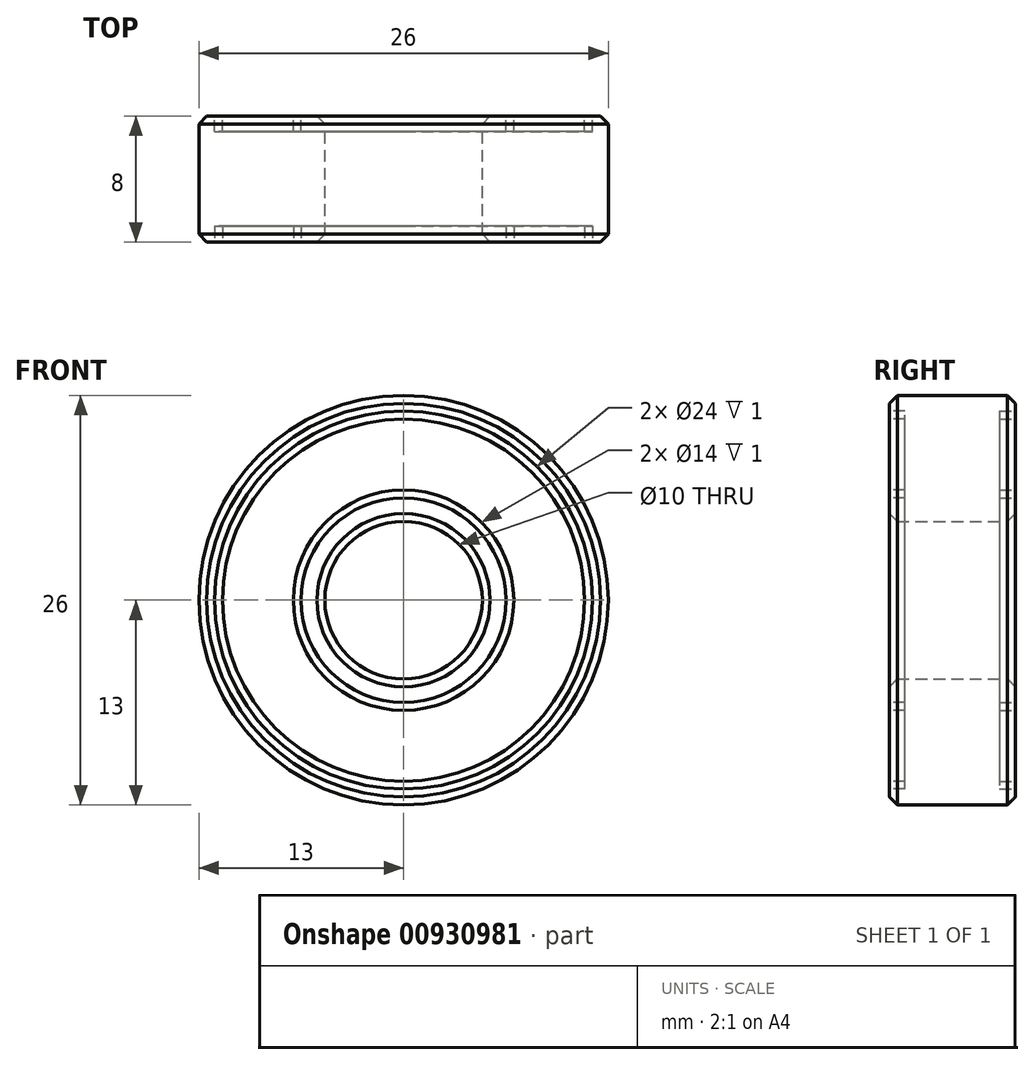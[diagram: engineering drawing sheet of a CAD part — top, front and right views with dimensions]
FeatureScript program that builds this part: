
annotation { "Feature Type Name" : "Feature", "Feature Type Description" : "" }
export const myFeature = defineFeature(function(context is Context, id is Id, definition is map)
    precondition{}
    {
        {
            var Q0;
            Q0=qCreatedBy(makeId("Front.planeOp"),FACE);
            var sketch = newSketch(context, id + "F0", { "sketchPlane" : qUnion([Q0])});
            skCircle(sketch, "E0", {"center": v(0, 0) * mm, "radius": 13 * mm});
            skCircle(sketch, "E1", {"center": v(0, 0) * mm, "radius": 5 * mm});
            skSolve(sketch);
        }
        {
            var Q0;
            Q0 = qSketchRegion(id + "F0", true);
            extrude(context, id + "F1", {"entities" : qUnion([Q0]), "depth" : 8 * mm, "offsetDistance" : 25 * mm});
        }
        {
            var Q0;
            Q0=makeQuery(id+"F1.opExtrude","CAP_FACE",FACE,{"disambiguationData":[OSD([sQuery(id+"F0.wireOp",EDGE,"E0"),sQuery(id+"F0.wireOp",EDGE,"E1")])],"isStart":false});
            var sketch = newSketch(context, id + "F2", { "sketchPlane" : qUnion([Q0])});
            skCircle(sketch, "E2", {"center": v(0, 0) * mm, "radius": 6.5 * mm});
            skCircle(sketch, "E3", {"center": v(0, 0) * mm, "radius": 7 * mm});
            skCircle(sketch, "E4", {"center": v(0, 0) * mm, "radius": 12 * mm});
            skCircle(sketch, "E5", {"center": v(0, 0) * mm, "radius": 11.5 * mm});
            skSolve(sketch);
        }
        {
            var Q0;
            Q0 = qSketchRegion(id + "F2", true);
            var Q1;
            Q1=makeQuery(id+"F2.imprint","IMPRINT",FACE,{"disambiguationData":[TD([[makeQuery(id+"F2.imprint","IMPRINT",EDGE,{"derivedFrom":sQuery(id+"F2.wireOp",EDGE,"E2")}),-1.0]])]});
            extrude(context, id + "F3", {"entities" : qUnion([Q0, Q1]), "operationType" : NewBodyOperationType.REMOVE, "oppositeDirection" : true, "depth" : 1 * mm, "offsetDistance" : 25 * mm});
        }
        {
            var Q0;
            Q0=makeQuery(id+"F1.opExtrude","CAP_FACE",FACE,{"disambiguationData":[OSD([sQuery(id+"F0.wireOp",EDGE,"E0"),sQuery(id+"F0.wireOp",EDGE,"E1")])],"isStart":true});
            var sketch = newSketch(context, id + "F4", { "sketchPlane" : qUnion([Q0])});
            skCircle(sketch, "E6", {"center": v(0, 0) * mm, "radius": 7 * mm});
            skCircle(sketch, "E7", {"center": v(0, 0) * mm, "radius": 6.5 * mm});
            skCircle(sketch, "E8", {"center": v(0, 0) * mm, "radius": 12 * mm});
            skCircle(sketch, "E9", {"center": v(0, 0) * mm, "radius": 11.5 * mm});
            skSolve(sketch);
        }
        {
            var Q0;
            Q0=makeQuery(id+"F4.imprint","IMPRINT",FACE,{"disambiguationData":[TD([[makeQuery(id+"F4.imprint","IMPRINT",EDGE,{"derivedFrom":sQuery(id+"F4.wireOp",EDGE,"E8")}),1.0]])]});
            var Q1;
            Q1=makeQuery(id+"F4.imprint","IMPRINT",FACE,{"disambiguationData":[TD([[makeQuery(id+"F4.imprint","IMPRINT",EDGE,{"derivedFrom":sQuery(id+"F4.wireOp",EDGE,"E6")}),1.0]])]});
            extrude(context, id + "F5", {"entities" : qUnion([Q0, Q1]), "operationType" : NewBodyOperationType.REMOVE, "oppositeDirection" : true, "depth" : 1 * mm, "offsetDistance" : 25 * mm});
        }
        {
            var Q0;
            Q0=makeQuery(id+"F1.opExtrude","CAP_EDGE",EDGE,{"disambiguationData":[OSD([sQuery(id+"F0.wireOp",EDGE,"E0")])],"isStart":true});
            var Q1;
            Q1=makeQuery(id+"F1.opExtrude","CAP_EDGE",EDGE,{"disambiguationData":[OSD([sQuery(id+"F0.wireOp",EDGE,"E1")])],"isStart":true});
            var Q2;
            Q2=makeQuery(id+"F1.opExtrude","CAP_EDGE",EDGE,{"disambiguationData":[OSD([sQuery(id+"F0.wireOp",EDGE,"E1")])],"isStart":false});
            var Q3;
            Q3=makeQuery(id+"F1.opExtrude","CAP_EDGE",EDGE,{"disambiguationData":[OSD([sQuery(id+"F0.wireOp",EDGE,"E0")])],"isStart":false});
            chamfer(context, id + "F6", {"entities" : qUnion([Q0, Q1, Q2, Q3]), "width" : 0.5 * mm, "tangentPropagation" : true});
        }
    });
